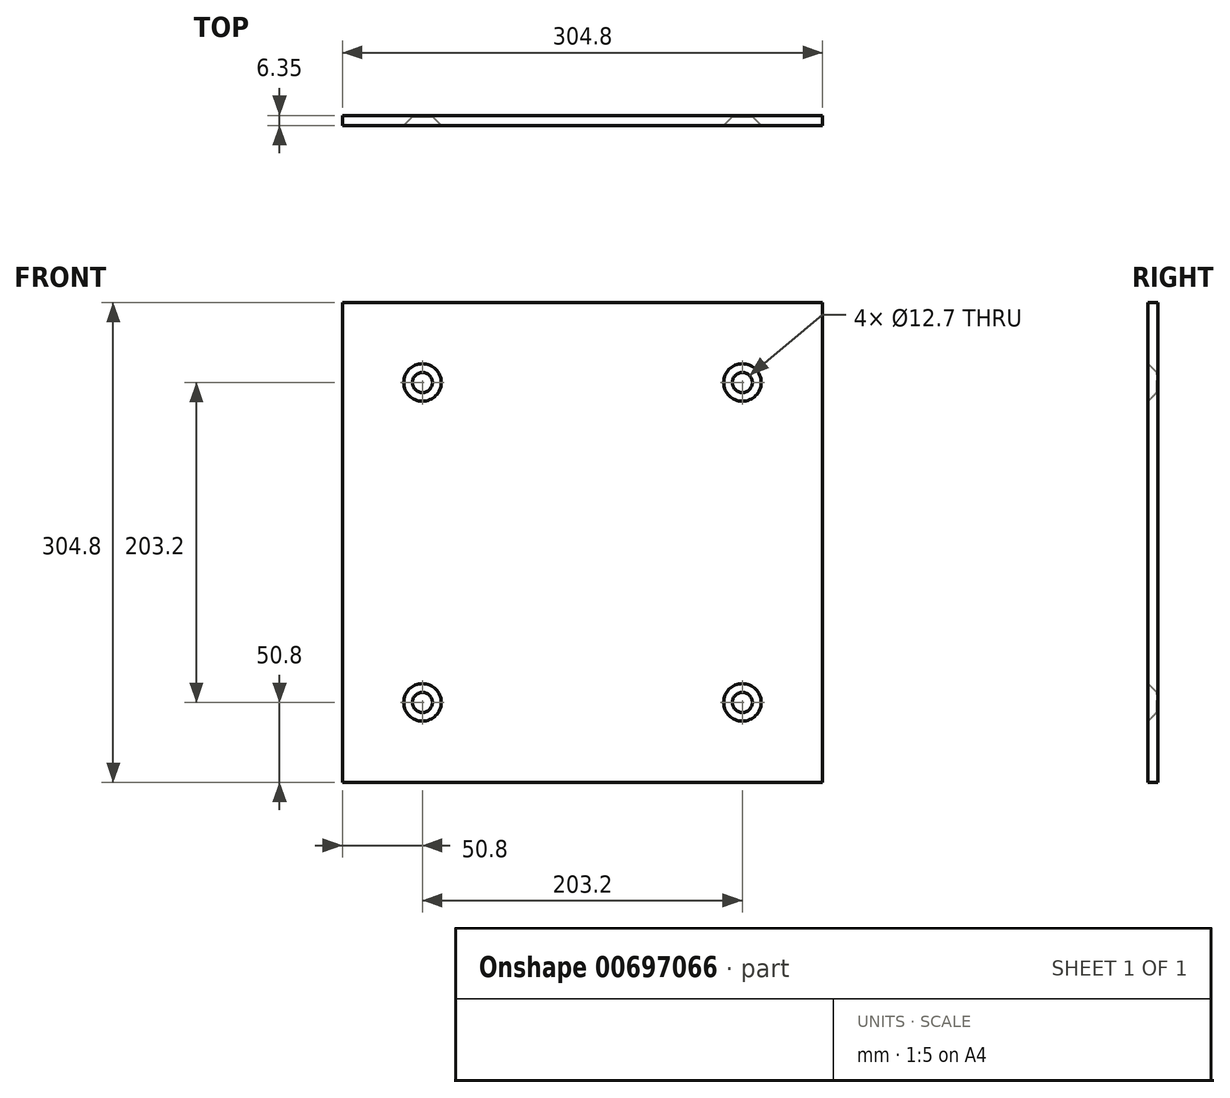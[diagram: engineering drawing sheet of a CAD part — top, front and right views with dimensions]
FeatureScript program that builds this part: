
annotation { "Feature Type Name" : "Feature", "Feature Type Description" : "" }
export const myFeature = defineFeature(function(context is Context, id is Id, definition is map)
    precondition{}
    {
        {
            var Q0;
            Q0=qCreatedBy(makeId("Front.planeOp"),FACE);
            var sketch = newSketch(context, id + "F0", { "sketchPlane" : qUnion([Q0])});
            skLineSegment(sketch, "E0.bottom", {"start": v(152.4, 152.4) * mm, "end": v(-152.4, 152.4) * mm});
            skLineSegment(sketch, "E0.top", {"start": v(152.4, -152.4) * mm, "end": v(-152.4, -152.4) * mm});
            skLineSegment(sketch, "E0.left", {"start": v(152.4, 152.4) * mm, "end": v(152.4, -152.4) * mm});
            skLineSegment(sketch, "E0.right", {"start": v(-152.4, 152.4) * mm, "end": v(-152.4, -152.4) * mm});
            skPoint(sketch, "E0.middle", {"position": v(0, 0) * mm});
            skSolve(sketch);
        }
        {
            var Q0;
            Q0 = qSketchRegion(id + "F0", true);
            extrude(context, id + "F1", {"entities" : qUnion([Q0]), "depth" : 6.35 * mm, "offsetDistance" : 25.4 * mm});
        }
        {
            var Q0;
            Q0=makeQuery(id+"F1.opExtrude","CAP_FACE",FACE,{"disambiguationData":[OSD([sQuery(id+"F0.wireOp",EDGE,"E0.bottom"),sQuery(id+"F0.wireOp",EDGE,"E0.top"),sQuery(id+"F0.wireOp",EDGE,"E0.left"),sQuery(id+"F0.wireOp",EDGE,"E0.right")])],"isStart":false});
            var sketch = newSketch(context, id + "F2", { "sketchPlane" : qUnion([Q0])});
            skLineSegment(sketch, "E1.bottom", {"start": v(101.6, 101.6) * mm, "end": v(-101.6, 101.6) * mm});
            skLineSegment(sketch, "E1.top", {"start": v(101.6, -101.6) * mm, "end": v(-101.6, -101.6) * mm});
            skLineSegment(sketch, "E1.left", {"start": v(101.6, 101.6) * mm, "end": v(101.6, -101.6) * mm});
            skLineSegment(sketch, "E1.right", {"start": v(-101.6, 101.6) * mm, "end": v(-101.6, -101.6) * mm});
            skPoint(sketch, "E1.middle", {"position": v(0, 0) * mm});
            skSolve(sketch);
        }
        {
            var Q0;
            Q0=sQuery(id+"F2.wireOp",VERTEX,"E1.right.start");
            var Q1;
            Q1=sQuery(id+"F2.wireOp",VERTEX,"E1.left.start");
            var Q2;
            Q2=sQuery(id+"F2.wireOp",VERTEX,"E1.left.end");
            var Q3;
            Q3=sQuery(id+"F2.wireOp",VERTEX,"E1.top.end");
            var Q4;
            Q4=makeQuery(id+"F1.opExtrude","SWEPT_BODY",BODY,{"disambiguationData":[OSD([sQuery(id+"F0.wireOp",EDGE,"E0.bottom"),sQuery(id+"F0.wireOp",EDGE,"E0.top"),sQuery(id+"F0.wireOp",EDGE,"E0.left"),sQuery(id+"F0.wireOp",EDGE,"E0.right")])]});
            hole(context, id + "F3", {"style" : HoleStyle.C_SINK, "endStyle" : HoleEndStyle.THROUGH, "holeDiameter" : 12.7 * mm, "cSinkDiameter" : 23.83 * mm, "cSinkAngle" : 90 * degree, "majorDiameter" : 6.35 * mm, "isTappedThrough" : true, "tappedDepth" : 12.7 * mm, "tapClearance" : 3, "startFromSketch" : true, "locations" : qUnion([Q0, Q1, Q2, Q3]), "scope" : qUnion([Q4])});
        }
    });
